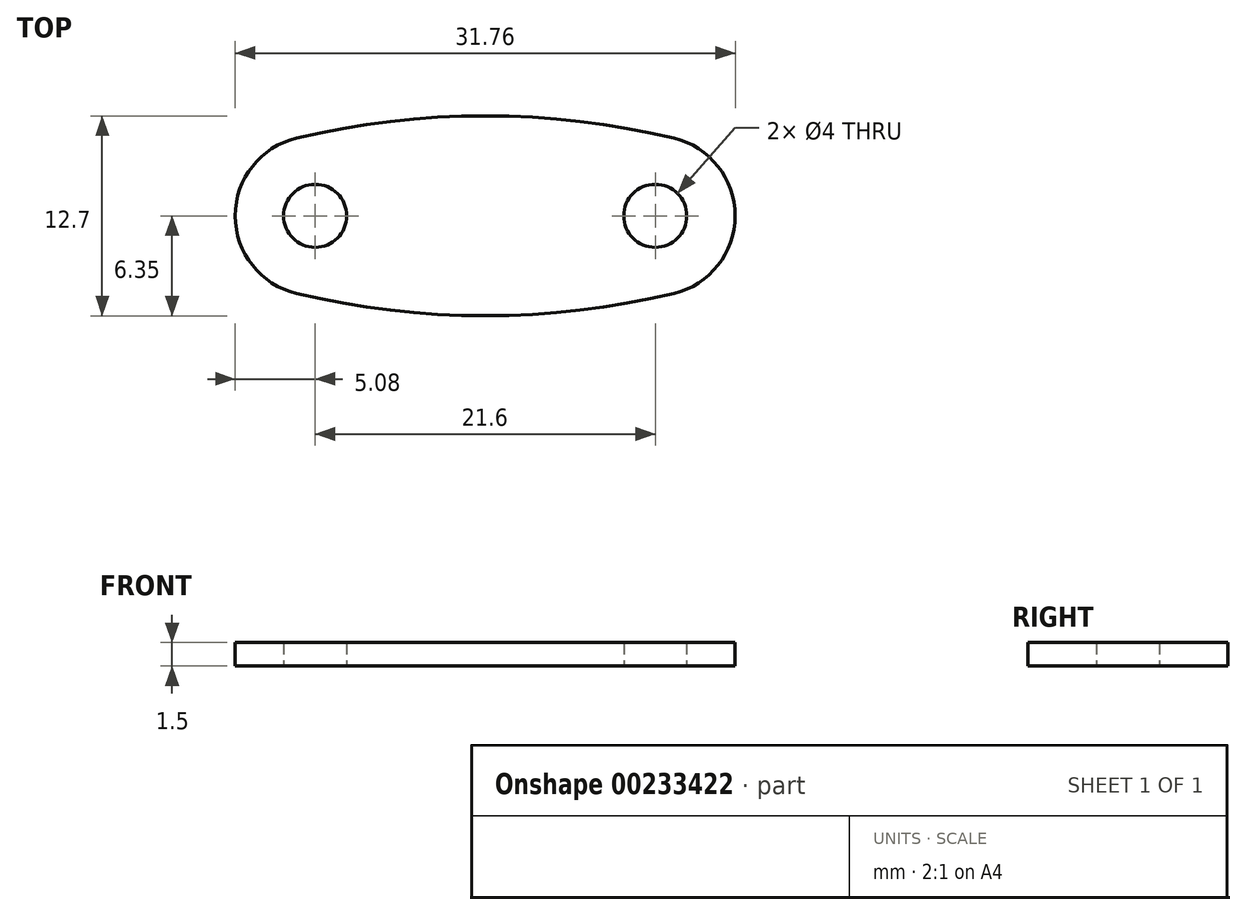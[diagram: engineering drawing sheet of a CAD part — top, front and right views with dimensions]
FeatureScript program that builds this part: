
annotation { "Feature Type Name" : "Feature", "Feature Type Description" : "" }
export const myFeature = defineFeature(function(context is Context, id is Id, definition is map)
    precondition{}
    {
        {
            var Q0;
            Q0=qCreatedBy(makeId("Top.planeOp"),FACE);
            var sketch = newSketch(context, id + "F0", { "sketchPlane" : qUnion([Q0])});
            skLineSegment(sketch, "E0", {"start": v(-15.87, 0) * mm, "end": v(15.87, 0) * mm, "construction": true});
            skLineSegment(sketch, "E1", {"start": v(0, 6.35) * mm, "end": v(0, -6.35) * mm, "construction": true});
            skCircle(sketch, "E2", {"center": v(-10.8, 0) * mm, "radius": 3.5 * mm, "construction": true});
            skArc(sketch, "E3", {"start": v(-11.98, 4.94) * mm, "mid": v(-15.87, 0) * mm, "end": v(-11.98, -4.94) * mm});
            skArc(sketch, "E4", {"start": v(0, 6.35) * mm, "mid": v(-6.03, 6) * mm, "end": v(-11.98, 4.94) * mm});
            skArc(sketch, "E5.MirrorCS", {"start": v(0, -6.35) * mm, "mid": v(-6.03, -6) * mm, "end": v(-11.98, -4.94) * mm});
            skArc(sketch, "E6.MirrorCS", {"start": v(0, 6.35) * mm, "mid": v(6.03, 6) * mm, "end": v(11.98, 4.94) * mm});
            skArc(sketch, "E7.MirrorCS", {"start": v(11.98, 4.94) * mm, "mid": v(15.87, 0) * mm, "end": v(11.98, -4.94) * mm});
            skCircle(sketch, "E8.MirrorC", {"center": v(10.8, 0) * mm, "radius": 3.5 * mm, "construction": true});
            skArc(sketch, "E9.MirrorCS", {"start": v(0, -6.35) * mm, "mid": v(6.03, -6) * mm, "end": v(11.98, -4.94) * mm});
            skCircle(sketch, "E10", {"center": v(-10.8, 0) * mm, "radius": 2 * mm});
            skCircle(sketch, "E11.MirrorC", {"center": v(10.8, 0) * mm, "radius": 2 * mm});
            skSolve(sketch);
        }
        {
            var Q0;
            Q0=makeQuery(id+"F0.imprint","IMPRINT",FACE,{"disambiguationData":[TD([[makeQuery(id+"F0.imprint","IMPRINT",EDGE,{"derivedFrom":sQuery(id+"F0.wireOp",EDGE,"E3")}),1.0]])]});
            extrude(context, id + "F1", {"entities" : qUnion([Q0]), "depth" : 1.5 * mm, "offsetDistance" : 25 * mm});
        }
    });
